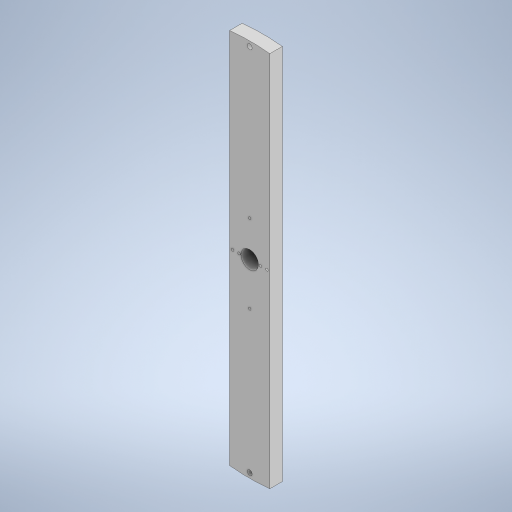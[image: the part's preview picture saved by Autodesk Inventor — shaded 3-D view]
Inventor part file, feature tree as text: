
AUTODESK INVENTOR PART (.ipt)
format: ipt  version: 2023.1 (Build 271208000, 208)  size: 257,536 bytes
history: native  units: mm
features: other x1, extrude x1, sketch x1
ambient origin geometry x8: Origin, YZ Plane, XZ Plane, XY Plane, X Axis, Y Axis, Z Axis, Center Point
bodies: Body1 (feature_tree)
feature tree (3):
  other  "솔리드1"
  extrude  "돌출1"  Depth=16.0mm
  sketch  "스케치1"
